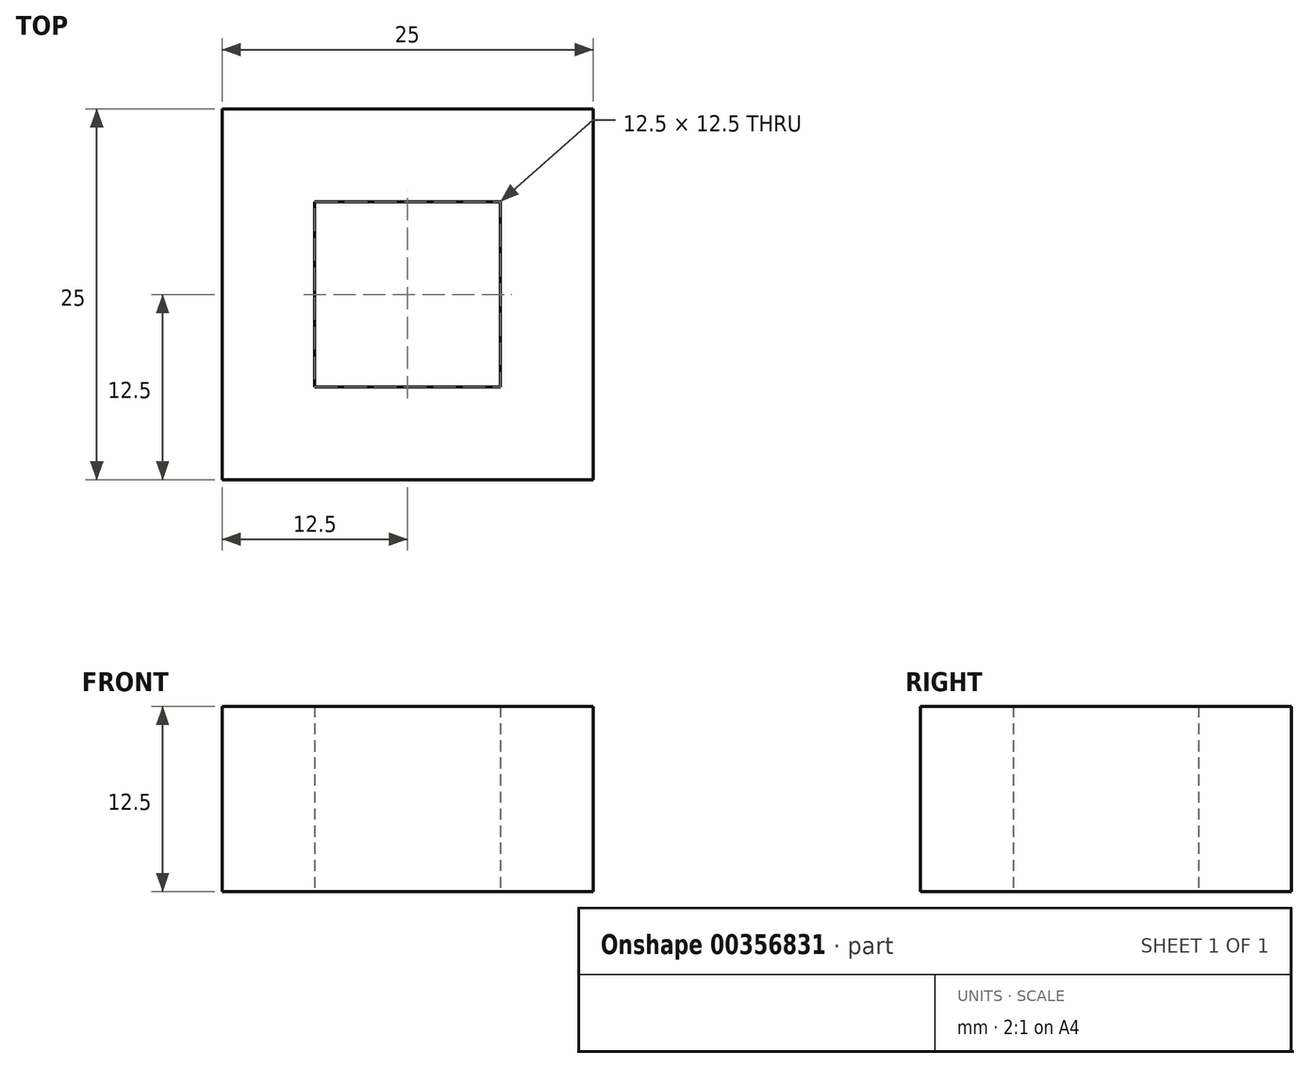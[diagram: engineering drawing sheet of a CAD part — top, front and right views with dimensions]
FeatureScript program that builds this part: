
annotation { "Feature Type Name" : "Feature", "Feature Type Description" : "" }
export const myFeature = defineFeature(function(context is Context, id is Id, definition is map)
    precondition{}
    {
        {
            assignVariable(context, id + "F0", {"name" : "Size", "anyValue" : 25});
        }
        {
            var Q0;
            Q0=qCreatedBy(makeId("Top.planeOp"),FACE);
            var sketch = newSketch(context, id + "F1", { "sketchPlane" : qUnion([Q0])});
            skLineSegment(sketch, "E0.bottom", {"start": v(0, 0) * mm, "end": v(25, 0) * mm});
            skLineSegment(sketch, "E0.top", {"start": v(0, 25) * mm, "end": v(25, 25) * mm});
            skLineSegment(sketch, "E0.left", {"start": v(0, 0) * mm, "end": v(0, 25) * mm});
            skLineSegment(sketch, "E0.right", {"start": v(25, 0) * mm, "end": v(25, 25) * mm});
            skLineSegment(sketch, "E1.0", {"start": v(6.25, 18.75) * mm, "end": v(18.75, 18.75) * mm});
            skLineSegment(sketch, "E1.1", {"start": v(6.25, 6.25) * mm, "end": v(6.25, 18.75) * mm});
            skLineSegment(sketch, "E1.2", {"start": v(6.25, 6.25) * mm, "end": v(18.75, 6.25) * mm});
            skLineSegment(sketch, "E1.3", {"start": v(18.75, 6.25) * mm, "end": v(18.75, 18.75) * mm});
            skSolve(sketch);
        }
        {
            var Q0;
            Q0=makeQuery(id+"F1.imprint","IMPRINT",FACE,{"disambiguationData":[TD([[makeQuery(id+"F1.imprint","IMPRINT",EDGE,{"derivedFrom":sQuery(id+"F1.wireOp",EDGE,"E0.bottom")}),1.0]])]});
            extrude(context, id + "F2", {"entities" : qUnion([Q0]), "depth" : (getVariable(context, 'Size') / 2) * mm});
        }
    });
